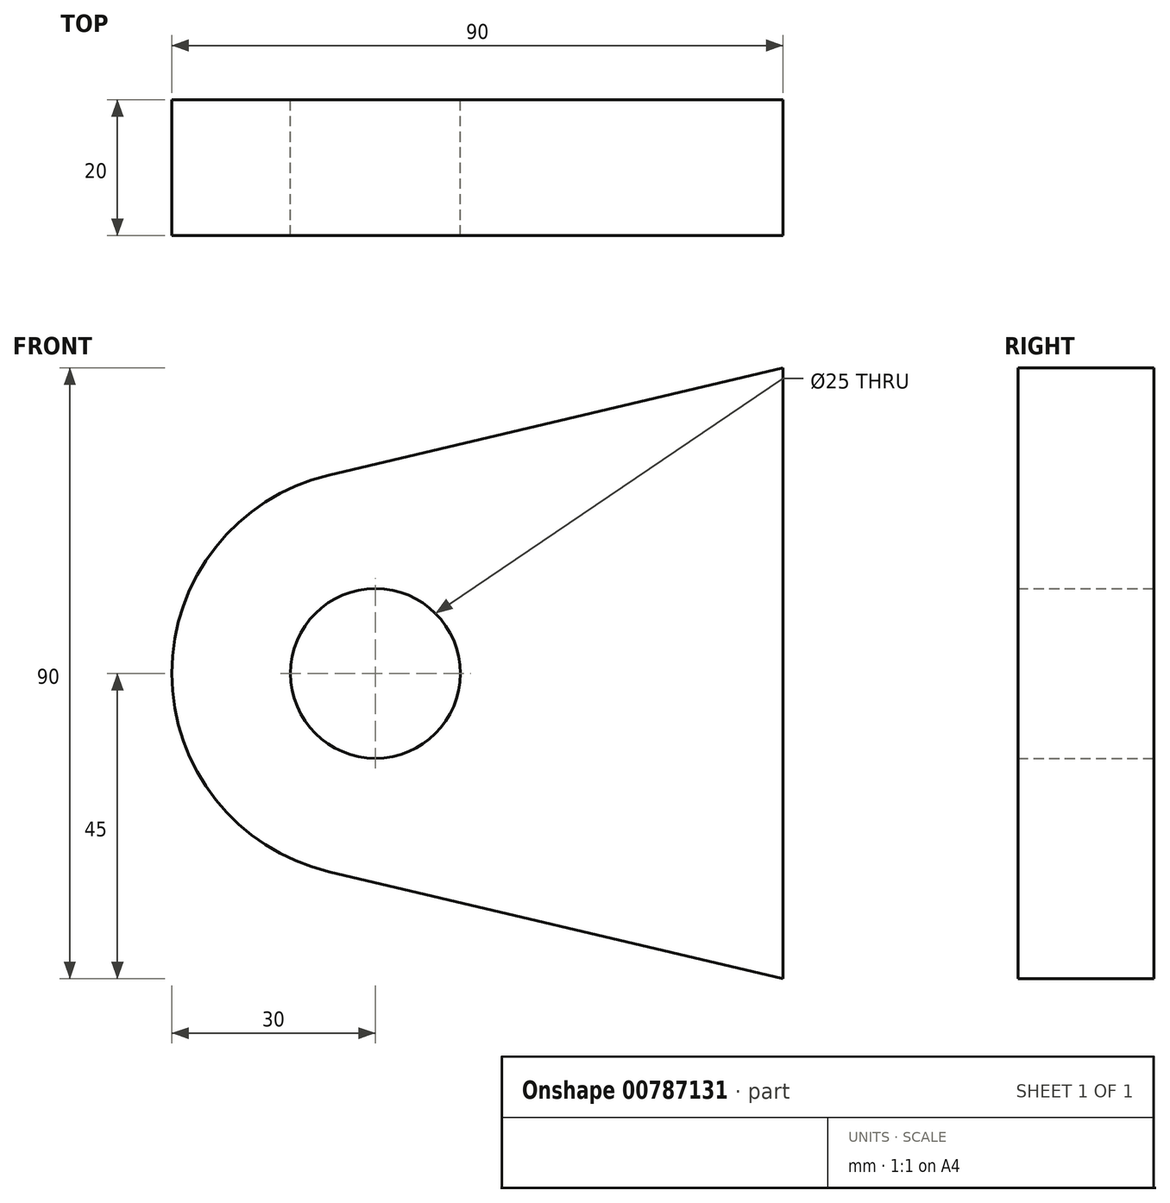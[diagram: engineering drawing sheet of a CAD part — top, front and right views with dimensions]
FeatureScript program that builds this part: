
annotation { "Feature Type Name" : "Feature", "Feature Type Description" : "" }
export const myFeature = defineFeature(function(context is Context, id is Id, definition is map)
    precondition{}
    {
        {
            var Q0;
            Q0=qCreatedBy(makeId("Front.planeOp"),FACE);
            var sketch = newSketch(context, id + "F0", { "sketchPlane" : qUnion([Q0])});
            skCircle(sketch, "E0", {"center": v(-60, 0) * mm, "radius": 12.5 * mm});
            skCircle(sketch, "E1", {"center": v(-60, 0) * mm, "radius": 30 * mm});
            skLineSegment(sketch, "E2", {"start": v(0, 45) * mm, "end": v(-66.9, 29.2) * mm});
            skLineSegment(sketch, "E3.MirrorCS", {"start": v(0, -45) * mm, "end": v(-66.9, -29.2) * mm});
            skLineSegment(sketch, "E4", {"start": v(0, 45) * mm, "end": v(0, -45) * mm});
            skSolve(sketch);
        }
        {
            var Q0;
            Q0=makeQuery(id+"F0.imprint","IMPRINT",FACE,{"disambiguationData":[TD([[makeQuery(id+"F0.imprint","IMPRINT",EDGE,{"derivedFrom":sQuery(id+"F0.wireOp",EDGE,"E0")}),-1.0]])]});
            var Q1;
            {var subQ0=sQuery(id+"F0.wireOp",EDGE,"E2");Q1=makeQuery(id+"F0.imprint","IMPRINT",FACE,{"disambiguationData":[TD([[makeQuery(id+"F0.imprint","IMPRINT",EDGE,{"derivedFrom":subQ0}),1.0]])]});}
            extrude(context, id + "F1", {"entities" : qUnion([Q0, Q1]), "depth" : 20 * mm, "offsetDistance" : 25 * mm});
        }
    });
